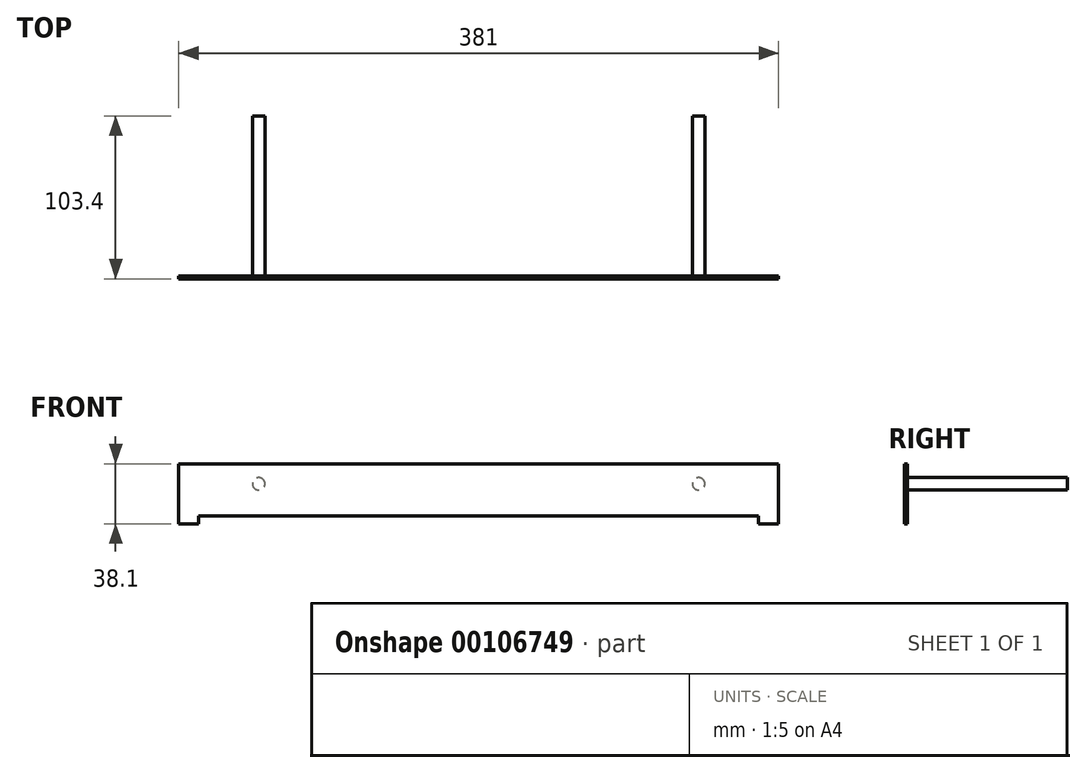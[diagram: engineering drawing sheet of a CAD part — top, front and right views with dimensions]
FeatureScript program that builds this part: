
annotation { "Feature Type Name" : "Feature", "Feature Type Description" : "" }
export const myFeature = defineFeature(function(context is Context, id is Id, definition is map)
    precondition{}
    {
        {
            var Q0;
            Q0=qCreatedBy(makeId("Front.planeOp"),FACE);
            var sketch = newSketch(context, id + "F0", { "sketchPlane" : qUnion([Q0])});
            skLineSegment(sketch, "E0.bottom", {"start": v(190.5, 19.05) * mm, "end": v(-190.5, 19.05) * mm});
            skLineSegment(sketch, "E0.top", {"start": v(190.5, -19.05) * mm, "end": v(177.8, -19.05) * mm});
            skLineSegment(sketch, "E0.left", {"start": v(190.5, 19.05) * mm, "end": v(190.5, -19.05) * mm});
            skLineSegment(sketch, "E0.right", {"start": v(-190.5, 19.05) * mm, "end": v(-190.5, -19.05) * mm});
            skPoint(sketch, "E0.middle", {"position": v(0, 0) * mm});
            skLineSegment(sketch, "E1", {"start": v(-177.8, -19.05) * mm, "end": v(-177.8, -13.97) * mm});
            skLineSegment(sketch, "E2", {"start": v(-177.8, -13.97) * mm, "end": v(177.8, -13.97) * mm});
            skLineSegment(sketch, "E3", {"start": v(177.8, -13.97) * mm, "end": v(177.8, -19.05) * mm});
            skLineSegment(sketch, "E4.trimOffspring", {"start": v(-177.8, -19.05) * mm, "end": v(-190.5, -19.05) * mm});
            skPoint(sketch, "E5", {"position": v(-139.7, 6.35) * mm});
            skPoint(sketch, "E6", {"position": v(139.7, 6.35) * mm});
            skCircle(sketch, "E7", {"center": v(-139.7, 6.35) * mm, "radius": 3.97 * mm});
            skCircle(sketch, "E8", {"center": v(139.7, 6.35) * mm, "radius": 3.97 * mm});
            skSolve(sketch);
        }
        {
            var Q0;
            Q0=makeQuery(id+"F0.imprint","IMPRINT",FACE,{"disambiguationData":[TD([[makeQuery(id+"F0.imprint","IMPRINT",EDGE,{"derivedFrom":sQuery(id+"F0.wireOp",EDGE,"E0.bottom")}),1.0]])]});
            var Q1;
            Q1=makeQuery(id+"F0.imprint","IMPRINT",FACE,{"disambiguationData":[TD([[makeQuery(id+"F0.imprint","IMPRINT",EDGE,{"derivedFrom":sQuery(id+"F0.wireOp",EDGE,"E7")}),1.0]])]});
            var Q2;
            Q2=makeQuery(id+"F0.imprint","IMPRINT",FACE,{"disambiguationData":[TD([[makeQuery(id+"F0.imprint","IMPRINT",EDGE,{"derivedFrom":sQuery(id+"F0.wireOp",EDGE,"E8")}),1.0]])]});
            extrude(context, id + "F1", {"entities" : qUnion([Q0, Q1, Q2]), "depth" : 1.8 * mm});
        }
        {
            var Q0;
            Q0=makeQuery(id+"F0.imprint","IMPRINT",FACE,{"disambiguationData":[TD([[makeQuery(id+"F0.imprint","IMPRINT",EDGE,{"derivedFrom":sQuery(id+"F0.wireOp",EDGE,"E7")}),1.0]])]});
            var Q1;
            Q1=makeQuery(id+"F0.imprint","IMPRINT",FACE,{"disambiguationData":[TD([[makeQuery(id+"F0.imprint","IMPRINT",EDGE,{"derivedFrom":sQuery(id+"F0.wireOp",EDGE,"E8")}),1.0]])]});
            extrude(context, id + "F2", {"entities" : qUnion([Q0, Q1]), "operationType" : NewBodyOperationType.ADD, "oppositeDirection" : true, "depth" : 101.6 * mm});
        }
    });
